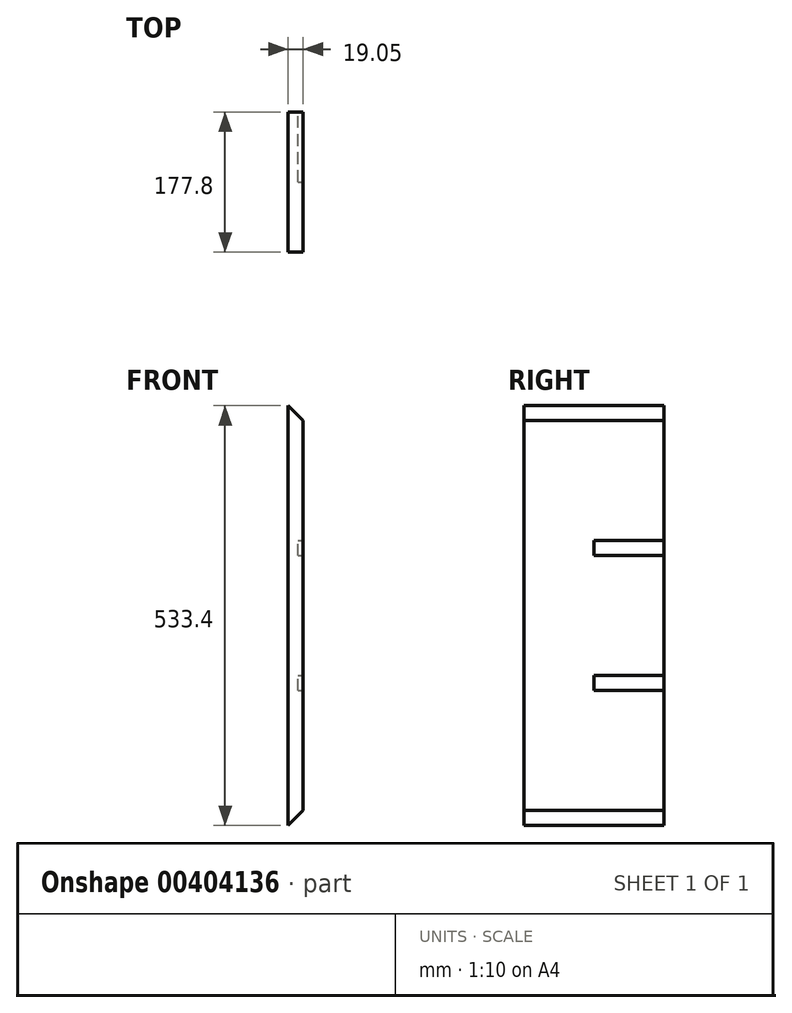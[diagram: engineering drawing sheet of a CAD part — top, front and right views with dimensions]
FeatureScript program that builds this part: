
annotation { "Feature Type Name" : "Feature", "Feature Type Description" : "" }
export const myFeature = defineFeature(function(context is Context, id is Id, definition is map)
    precondition{}
    {
        {
            var Q0;
            Q0=qCreatedBy(makeId("Front.planeOp"),FACE);
            var sketch = newSketch(context, id + "F0", { "sketchPlane" : qUnion([Q0])});
            skLineSegment(sketch, "E0.left", {"start": v(0, 0) * mm, "end": v(0, 533.4) * mm});
            skLineSegment(sketch, "E0.right", {"start": v(19.05, 19.05) * mm, "end": v(19.05, 514.35) * mm});
            skLineSegment(sketch, "E1", {"start": v(0, 533.4) * mm, "end": v(19.05, 514.35) * mm});
            skLineSegment(sketch, "E2", {"start": v(0, 0) * mm, "end": v(19.05, 19.05) * mm});
            skSolve(sketch);
        }
        {
            var Q0;
            Q0 = qSketchRegion(id + "F0", true);
            extrude(context, id + "F1", {"entities" : qUnion([Q0]), "endBound" : BoundingType.SYMMETRIC, "depth" : 177.8 * mm});
        }
        {
            var Q0;
            Q0=makeQuery(id+"F1.opExtrude","SWEPT_FACE",FACE,{"disambiguationData":[OSD([sQuery(id+"F0.wireOp",EDGE,"E0.right")])]});
            var sketch = newSketch(context, id + "F2", { "sketchPlane" : qUnion([Q0])});
            skLineSegment(sketch, "E3.bottom", {"start": v(0, 190.5) * mm, "end": v(88.9, 190.5) * mm});
            skLineSegment(sketch, "E3.top", {"start": v(0, 171.45) * mm, "end": v(88.9, 171.45) * mm});
            skLineSegment(sketch, "E3.left", {"start": v(0, 171.45) * mm, "end": v(0, 190.5) * mm});
            skLineSegment(sketch, "E3.right", {"start": v(88.9, 171.45) * mm, "end": v(88.9, 190.5) * mm});
            skLineSegment(sketch, "E4.bottom", {"start": v(0, 361.95) * mm, "end": v(88.9, 361.95) * mm});
            skLineSegment(sketch, "E4.top", {"start": v(0, 342.9) * mm, "end": v(88.9, 342.9) * mm});
            skLineSegment(sketch, "E4.left", {"start": v(0, 361.95) * mm, "end": v(0, 342.9) * mm});
            skLineSegment(sketch, "E4.right", {"start": v(88.9, 361.95) * mm, "end": v(88.9, 342.9) * mm});
            skSolve(sketch);
        }
        {
            var Q0;
            Q0 = qSketchRegion(id + "F2", true);
            extrude(context, id + "F3", {"entities" : qUnion([Q0]), "operationType" : NewBodyOperationType.REMOVE, "oppositeDirection" : true, "depth" : 6.35 * mm});
        }
    });
